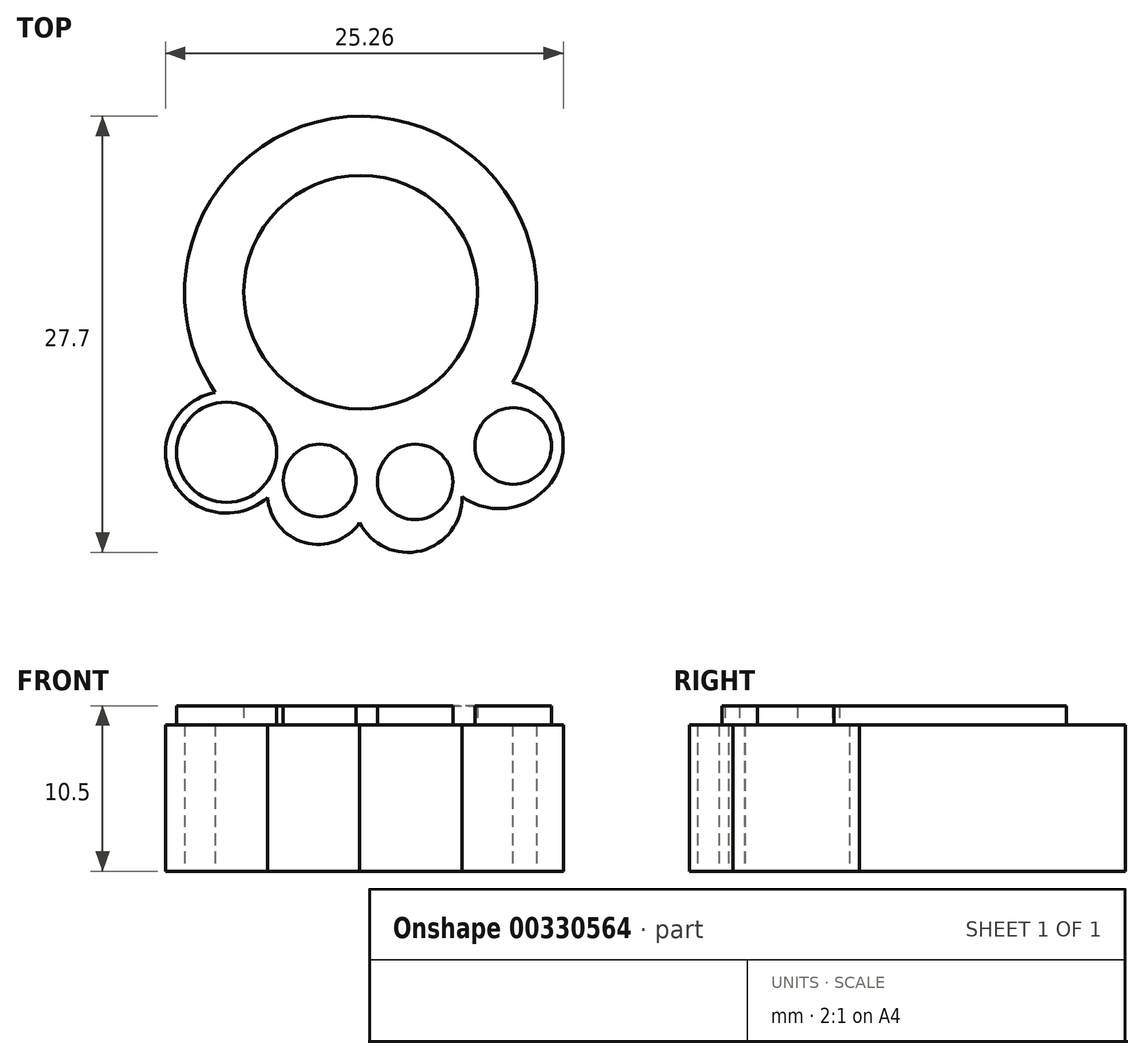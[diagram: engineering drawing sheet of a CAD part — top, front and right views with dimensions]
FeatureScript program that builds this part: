
annotation { "Feature Type Name" : "Feature", "Feature Type Description" : "" }
export const myFeature = defineFeature(function(context is Context, id is Id, definition is map)
    precondition{}
    {
        {
            var Q0;
            Q0=qCreatedBy(makeId("Top.planeOp"),FACE);
            var sketch = newSketch(context, id + "F0", { "sketchPlane" : qUnion([Q0])});
            skArc(sketch, "E0", {"start": v(-16.94, 33.42) * mm, "mid": v(-27.81, 42.65) * mm, "end": v(-38.9, 33.67) * mm});
            skArc(sketch, "E1", {"start": v(-38.9, 33.67) * mm, "mid": v(-28.07, 20.23) * mm, "end": v(-16.94, 33.42) * mm});
            skArc(sketch, "E2", {"start": v(-37.18, 25.1) * mm, "mid": v(-38.95, 18.35) * mm, "end": v(-32.6, 21.25) * mm});
            skArc(sketch, "E3", {"start": v(-32.6, 21.25) * mm, "mid": v(-31.3, 15.53) * mm, "end": v(-27.81, 20.23) * mm});
            skPoint(sketch, "E3.endSnap0", {"position": v(-28.07, 20.23) * mm});
            skArc(sketch, "E4", {"start": v(-27.81, 20.23) * mm, "mid": v(-24.16, 15.04) * mm, "end": v(-23.16, 21.3) * mm});
            skArc(sketch, "E5", {"start": v(-23.16, 21.3) * mm, "mid": v(-16.4, 18.78) * mm, "end": v(-18.3, 25.75) * mm});
            skSolve(sketch);
        }
        {
            var Q0;
            Q0 = qSketchRegion(id + "F0", true);
            extrude(context, id + "F1", {"entities" : qUnion([Q0]), "depth" : 9.3 * mm});
        }
        {
            var Q0;
            Q0=makeQuery(id+"F1.opExtrude","CAP_FACE",FACE,{"disambiguationData":[OSD([sQuery(id+"F0.wireOp",EDGE,"E0"),sQuery(id+"F0.wireOp",EDGE,"E1"),sQuery(id+"F0.wireOp",EDGE,"E2"),sQuery(id+"F0.wireOp",EDGE,"E3"),sQuery(id+"F0.wireOp",EDGE,"E4"),sQuery(id+"F0.wireOp",EDGE,"E5")])],"isStart":false});
            var sketch = newSketch(context, id + "F2", { "sketchPlane" : qUnion([Q0])});
            skCircle(sketch, "E6", {"center": v(-27.94, 31.48) * mm, "radius": 7.42 * mm});
            skCircle(sketch, "E7", {"center": v(-36.46, 21.3) * mm, "radius": 3.18 * mm});
            skCircle(sketch, "E8", {"center": v(-30.55, 19.52) * mm, "radius": 2.31 * mm});
            skCircle(sketch, "E9", {"center": v(-24.48, 19.43) * mm, "radius": 2.4 * mm});
            skCircle(sketch, "E10", {"center": v(-18.25, 21.7) * mm, "radius": 2.43 * mm});
            skSolve(sketch);
        }
        {
            var Q0;
            Q0=makeQuery(id+"F2.imprint","IMPRINT",FACE,{"disambiguationData":[TD([[makeQuery(id+"F2.imprint","IMPRINT",EDGE,{"derivedFrom":sQuery(id+"F2.wireOp",EDGE,"E6")}),1.0]])]});
            var Q1;
            Q1=makeQuery(id+"F2.imprint","IMPRINT",FACE,{"disambiguationData":[TD([[makeQuery(id+"F2.imprint","IMPRINT",EDGE,{"derivedFrom":sQuery(id+"F2.wireOp",EDGE,"E7")}),1.0]])]});
            var Q2;
            Q2=makeQuery(id+"F2.imprint","IMPRINT",FACE,{"disambiguationData":[TD([[makeQuery(id+"F2.imprint","IMPRINT",EDGE,{"derivedFrom":sQuery(id+"F2.wireOp",EDGE,"E8")}),1.0]])]});
            var Q3;
            Q3=makeQuery(id+"F2.imprint","IMPRINT",FACE,{"disambiguationData":[TD([[makeQuery(id+"F2.imprint","IMPRINT",EDGE,{"derivedFrom":sQuery(id+"F2.wireOp",EDGE,"E9")}),1.0]])]});
            var Q4;
            Q4=makeQuery(id+"F2.imprint","IMPRINT",FACE,{"disambiguationData":[TD([[makeQuery(id+"F2.imprint","IMPRINT",EDGE,{"derivedFrom":sQuery(id+"F2.wireOp",EDGE,"E10")}),1.0]])]});
            extrude(context, id + "F3", {"entities" : qUnion([Q0, Q1, Q2, Q3, Q4]), "operationType" : NewBodyOperationType.ADD, "depth" : 1.2 * mm});
        }
    });
